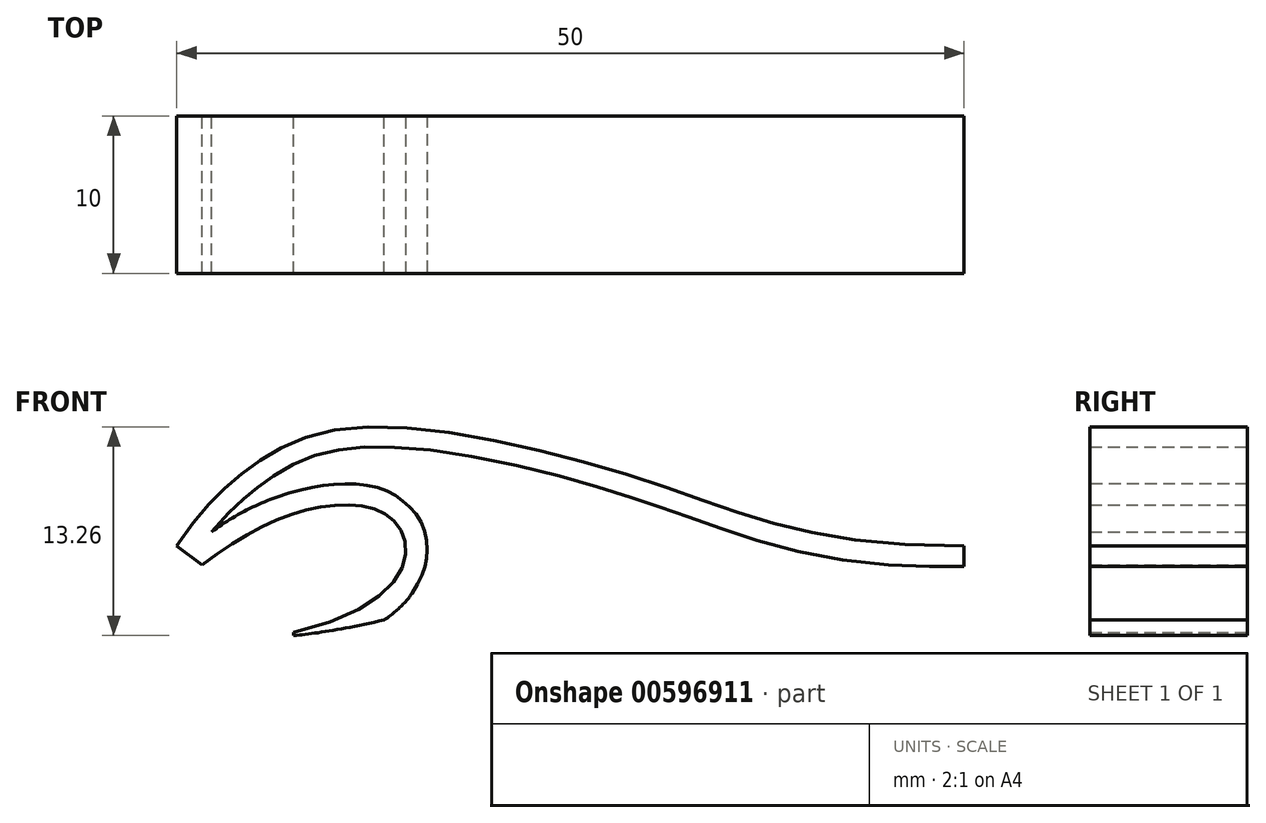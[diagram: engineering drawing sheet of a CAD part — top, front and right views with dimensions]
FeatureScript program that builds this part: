
annotation { "Feature Type Name" : "Feature", "Feature Type Description" : "" }
export const myFeature = defineFeature(function(context is Context, id is Id, definition is map)
    precondition{}
    {
        {
            var Q0;
            Q0=qCreatedBy(makeId("Front.planeOp"),FACE);
            var sketch = newSketch(context, id + "F0", { "sketchPlane" : qUnion([Q0])});
            skLineSegment(sketch, "E0.bottom", {"start": v(25, 7.5) * mm, "end": v(-25, 7.5) * mm, "construction": true});
            skLineSegment(sketch, "E0.top", {"start": v(25, -7.5) * mm, "end": v(-25, -7.5) * mm, "construction": true});
            skLineSegment(sketch, "E0.left", {"start": v(25, 7.5) * mm, "end": v(25, -7.5) * mm, "construction": true});
            skLineSegment(sketch, "E0.right", {"start": v(-25, 7.5) * mm, "end": v(-25, -7.5) * mm, "construction": true});
            skPoint(sketch, "E0.middle", {"position": v(0, 0) * mm});
            skFitSpline(sketch, "E1", {"points": [v(-25, 0) * mm, v(-20.8, 4.63) * mm, v(-13.93, 7.5) * mm, v(5.47, 3.93) * mm, v(25, 0) * mm], "startDerivative": vector(24.84, 37.46) * mm, "endDerivative": vector(93.66, 0) * mm});
            skLineSegment(sketch, "E2", {"start": v(-25, 0) * mm, "end": v(-23.4, -1.2) * mm});
            skFitSpline(sketch, "E3", {"points": [v(-23.4, -1.2) * mm, v(-15.65, 2.51) * mm, v(-11.03, 1.4) * mm, v(-17.57, -5.5) * mm], "startDerivative": vector(21.85, 16.88) * mm, "endDerivative": vector(-59.4, -14.42) * mm});
            skLineSegment(sketch, "E4", {"start": v(-17.57, -5.5) * mm, "end": v(-17.57, -7) * mm});
            skFitSpline(sketch, "E5", {"points": [v(-17.57, -7) * mm, v(7.5, -1.83) * mm, v(25, -7) * mm], "startDerivative": vector(44.44, 5.4) * mm, "endDerivative": vector(33.41, -25.5) * mm});
            skLineSegment(sketch, "E6", {"start": v(25, 0) * mm, "end": v(25, -7) * mm});
            skFitSpline(sketch, "E7.0", {"points": [v(-23.92, -0.72) * mm, v(-23.42, 0.03) * mm, v(-22.73, 0.96) * mm, v(-21.86, 1.95) * mm, v(-21.2, 2.6) * mm, v(-20.62, 3.12) * mm, v(-20.13, 3.52) * mm, v(-19.61, 3.92) * mm, v(-18.95, 4.4) * mm, v(-18.1, 4.92) * mm, v(-17.17, 5.39) * mm, v(-16.13, 5.77) * mm, v(-14.96, 6.07) * mm, v(-13.62, 6.25) * mm, v(-12.07, 6.3) * mm, v(-9.77, 6.18) * mm, v(-6.56, 5.75) * mm, v(-2.48, 4.9) * mm, v(0.9, 4) * mm, v(3.46, 3.22) * mm, v(5.26, 2.63) * mm, v(6.94, 2.05) * mm, v(9.1, 1.28) * mm, v(11.77, 0.37) * mm, v(15.3, -0.53) * mm, v(19.52, -1.15) * mm, v(23.02, -1.3) * mm, v(25, -1.3) * mm]});
            skFitSpline(sketch, "E7.1", {"points": [v(-24.2, -0.17) * mm, v(-23.25, 0.56) * mm, v(-21.32, 1.87) * mm, v(-18.89, 3.02) * mm, v(-16.92, 3.62) * mm, v(-15.44, 3.88) * mm, v(-13.95, 3.95) * mm, v(-12.5, 3.77) * mm, v(-11.35, 3.34) * mm, v(-10.53, 2.77) * mm, v(-9.8, 2.03) * mm, v(-9.3, 1.06) * mm, v(-9.12, -0.06) * mm, v(-9.17, -0.96) * mm, v(-9.44, -1.86) * mm, v(-10.07, -3.03) * mm, v(-11.37, -4.36) * mm, v(-13.75, -5.72) * mm, v(-15.97, -6.45) * mm, v(-17.27, -6.76) * mm]});
            skFitSpline(sketch, "E7.2", {"points": [v(-17.73, -5.7) * mm, v(-15.94, -5.5) * mm, v(-12.2, -4.78) * mm, v(-6.32, -3.26) * mm, v(-1.36, -1.98) * mm, v(2.57, -1.15) * mm, v(5.48, -0.69) * mm, v(8.34, -0.44) * mm, v(11.1, -0.46) * mm, v(13.78, -0.73) * mm, v(17.23, -1.43) * mm, v(21.31, -2.96) * mm, v(24.33, -4.86) * mm, v(25.79, -5.97) * mm]});
            skLineSegment(sketch, "E8", {"start": v(-19.38, 4.09) * mm, "end": v(-18.66, 3.04) * mm});
            skLineSegment(sketch, "E9", {"start": v(-10.1, -2.95) * mm, "end": v(-9.33, -4.03) * mm});
            skLineSegment(sketch, "E10", {"start": v(22.84, -1.27) * mm, "end": v(21.5, -3.25) * mm});
            skSolve(sketch);
        }
        {
            var Q0;
            Q0=makeQuery(id+"F0.imprint","IMPRINT",FACE,{"disambiguationData":[TD([[makeQuery(id+"F0.imprint","IMPRINT",EDGE,{"derivedFrom":sQuery(id+"F0.wireOp",EDGE,"E1")}),-1.0]])]});
            extrude(context, id + "F1", {"entities" : qUnion([Q0]), "depth" : 10 * mm, "offsetDistance" : 25 * mm});
        }
    });
